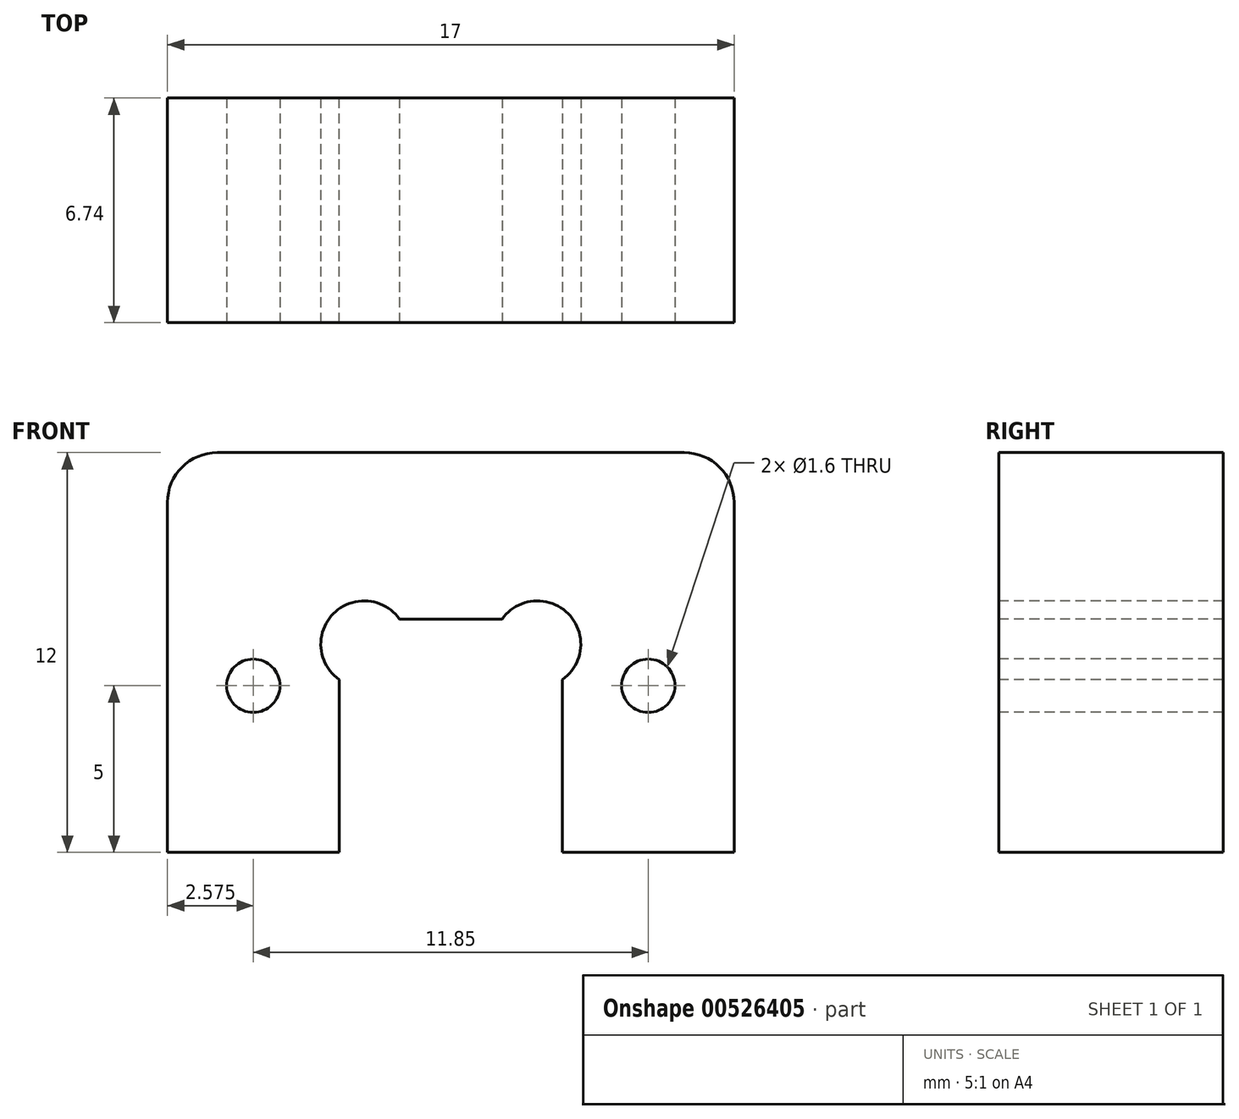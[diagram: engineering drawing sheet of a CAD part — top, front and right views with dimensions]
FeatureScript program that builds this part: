
annotation { "Feature Type Name" : "Feature", "Feature Type Description" : "" }
export const myFeature = defineFeature(function(context is Context, id is Id, definition is map)
    precondition{}
    {
        {
            var Q0;
            Q0=qCreatedBy(makeId("Front.planeOp"),FACE);
            var sketch = newSketch(context, id + "F0", { "sketchPlane" : qUnion([Q0])});
            skLineSegment(sketch, "E0.bottom", {"start": v(-7, 2.5) * mm, "end": v(7, 2.5) * mm});
            skLineSegment(sketch, "E0.top", {"start": v(-8.5, -2.5) * mm, "end": v(8.5, -2.5) * mm});
            skLineSegment(sketch, "E0.left", {"start": v(-8.5, 1) * mm, "end": v(-8.5, -2.5) * mm});
            skLineSegment(sketch, "E0.right", {"start": v(8.5, 1) * mm, "end": v(8.5, -2.5) * mm});
            skPoint(sketch, "E0.middle", {"position": v(0, 0) * mm});
            skLineSegment(sketch, "E1.top", {"start": v(-8.5, -9.5) * mm, "end": v(-3.35, -9.5) * mm});
            skLineSegment(sketch, "E1.left", {"start": v(-8.5, -2.5) * mm, "end": v(-8.5, -9.5) * mm});
            skLineSegment(sketch, "E1.right", {"start": v(-3.35, -2.5) * mm, "end": v(-3.35, -9.5) * mm});
            skLineSegment(sketch, "E2.bottom", {"start": v(8.5, -2.5) * mm, "end": v(3.35, -2.5) * mm});
            skLineSegment(sketch, "E2.top", {"start": v(8.5, -9.5) * mm, "end": v(3.35, -9.5) * mm});
            skLineSegment(sketch, "E2.left", {"start": v(8.5, -2.5) * mm, "end": v(8.5, -9.5) * mm});
            skLineSegment(sketch, "E2.right", {"start": v(3.35, -2.5) * mm, "end": v(3.35, -9.5) * mm});
            skPoint(sketch, "E3.visualSharp", {"position": v(-8.5, 2.5) * mm});
            skArc(sketch, "E3.filletArc", {"start": v(-7, 2.5) * mm, "mid": v(-8.06, 2.06) * mm, "end": v(-8.5, 1) * mm});
            skPoint(sketch, "E4.visualSharp", {"position": v(8.5, 2.5) * mm});
            skArc(sketch, "E4.filletArc", {"start": v(8.5, 1) * mm, "mid": v(8.06, 2.06) * mm, "end": v(7, 2.5) * mm});
            skSolve(sketch);
        }
        {
            var Q0;
            Q0 = qSketchRegion(id + "F0", true);
            extrude(context, id + "F1", {"entities" : qUnion([Q0]), "depth" : 6.74 * mm, "offsetDistance" : 25 * mm});
        }
        {
            var Q0;
            Q0=makeQuery(id+"F1.opExtrude","CAP_FACE",FACE,{"disambiguationData":[OSD([sQuery(id+"F0.wireOp",EDGE,"E0.bottom"),sQuery(id+"F0.wireOp",EDGE,"E0.top"),sQuery(id+"F0.wireOp",EDGE,"E0.left"),sQuery(id+"F0.wireOp",EDGE,"E0.right"),sQuery(id+"F0.wireOp",EDGE,"E1.top"),sQuery(id+"F0.wireOp",EDGE,"E1.left"),sQuery(id+"F0.wireOp",EDGE,"E1.right"),sQuery(id+"F0.wireOp",EDGE,"E2.top"),sQuery(id+"F0.wireOp",EDGE,"E2.left"),sQuery(id+"F0.wireOp",EDGE,"E2.right"),sQuery(id+"F0.wireOp",EDGE,"E3.filletArc"),sQuery(id+"F0.wireOp",EDGE,"E4.filletArc")])],"isStart":false});
            var sketch = newSketch(context, id + "F2", { "sketchPlane" : qUnion([Q0])});
            skCircle(sketch, "E5", {"center": v(-2.6, -3.25) * mm, "radius": 1.3 * mm});
            skCircle(sketch, "E6.MirrorC", {"center": v(2.6, -3.25) * mm, "radius": 1.3 * mm});
            skSolve(sketch);
        }
        {
            var Q0;
            Q0 = qSketchRegion(id + "F2", true);
            extrude(context, id + "F3", {"entities" : qUnion([Q0]), "operationType" : NewBodyOperationType.REMOVE, "oppositeDirection" : true, "depth" : 25 * mm, "offsetDistance" : 25 * mm});
        }
        {
            var Q0;
            Q0=makeQuery(id+"F1.opExtrude","CAP_FACE",FACE,{"disambiguationData":[OSD([sQuery(id+"F0.wireOp",EDGE,"E0.bottom"),sQuery(id+"F0.wireOp",EDGE,"E0.top"),sQuery(id+"F0.wireOp",EDGE,"E0.left"),sQuery(id+"F0.wireOp",EDGE,"E0.right"),sQuery(id+"F0.wireOp",EDGE,"E1.top"),sQuery(id+"F0.wireOp",EDGE,"E1.left"),sQuery(id+"F0.wireOp",EDGE,"E1.right"),sQuery(id+"F0.wireOp",EDGE,"E2.top"),sQuery(id+"F0.wireOp",EDGE,"E2.left"),sQuery(id+"F0.wireOp",EDGE,"E2.right"),sQuery(id+"F0.wireOp",EDGE,"E3.filletArc"),sQuery(id+"F0.wireOp",EDGE,"E4.filletArc")])],"isStart":false});
            var sketch = newSketch(context, id + "F4", { "sketchPlane" : qUnion([Q0])});
            skCircle(sketch, "E7", {"center": v(-5.93, -4.5) * mm, "radius": 0.8 * mm});
            skLineSegment(sketch, "E8", {"start": v(-5.92, -9.5) * mm, "end": v(-5.93, 4.72) * mm, "construction": true});
            skCircle(sketch, "E9.MirrorC", {"center": v(5.93, -4.5) * mm, "radius": 0.8 * mm});
            skSolve(sketch);
        }
        {
            var Q0;
            Q0 = qSketchRegion(id + "F4", true);
            var Q1;
            Q1=sQuery(id+"F4.wireOp",EDGE,"E7");
            var Q2;
            Q2=sQuery(id+"F4.wireOp",EDGE,"E9.MirrorC");
            extrude(context, id + "F5", {"entities" : qUnion([Q0]), "operationType" : NewBodyOperationType.REMOVE, "surfaceEntities" : qUnion([Q1, Q2]), "endBound" : BoundingType.THROUGH_ALL, "oppositeDirection" : true, "depth" : 7.64 * mm, "offsetDistance" : 25 * mm});
        }
    });
